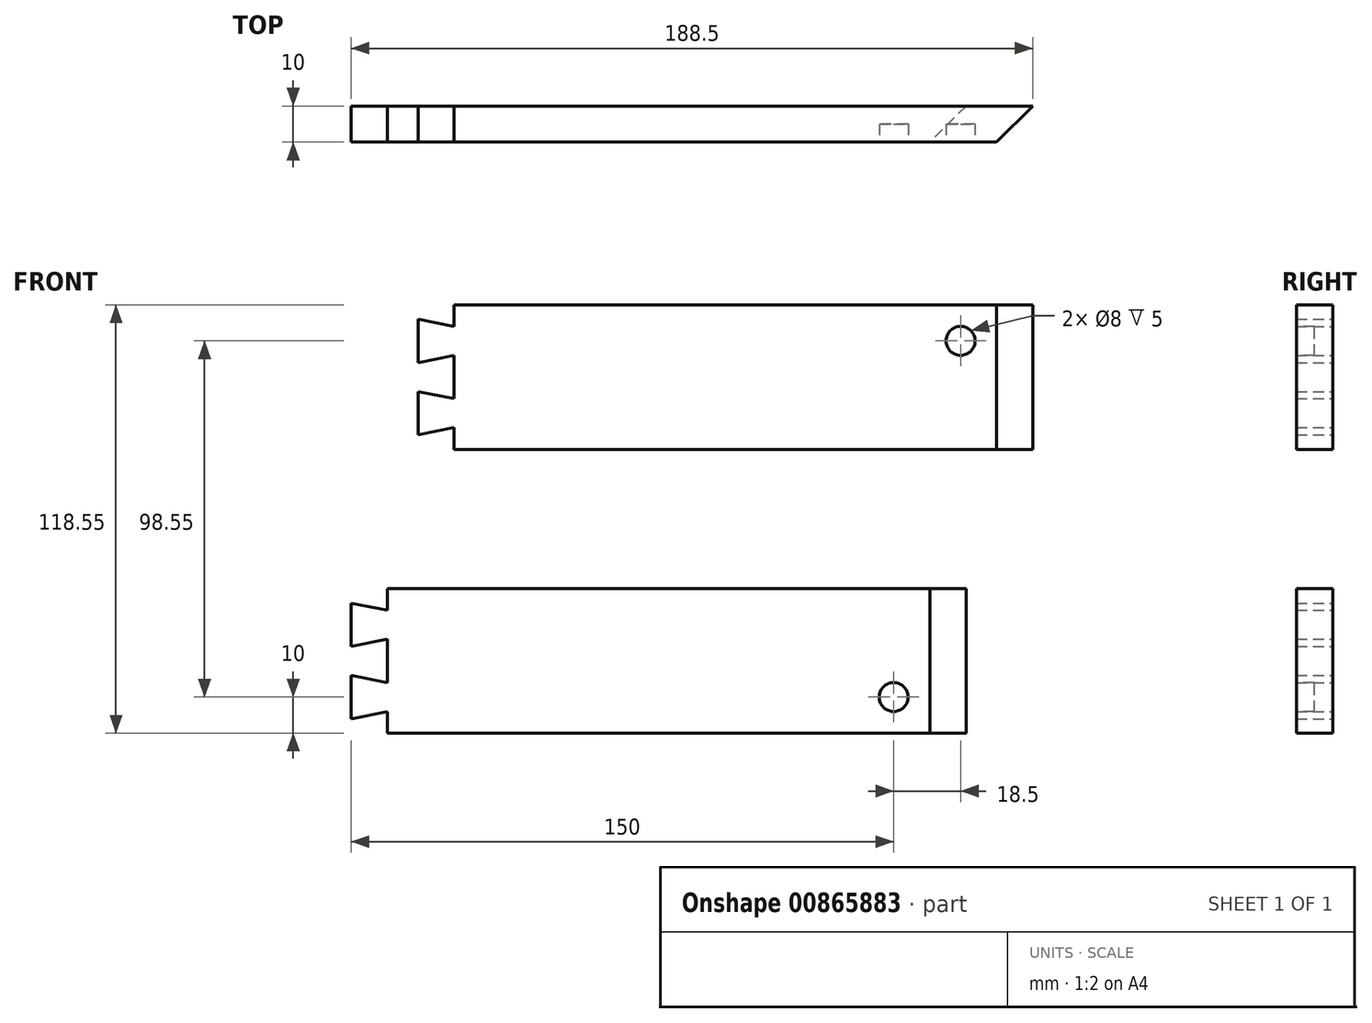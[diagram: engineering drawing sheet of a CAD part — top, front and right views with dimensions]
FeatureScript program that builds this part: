
annotation { "Feature Type Name" : "Feature", "Feature Type Description" : "" }
export const myFeature = defineFeature(function(context is Context, id is Id, definition is map)
    precondition{}
    {
        {
            var Q0;
            Q0=qCreatedBy(makeId("Front.planeOp"),FACE);
            var sketch = newSketch(context, id + "F0", { "sketchPlane" : qUnion([Q0])});
            skLineSegment(sketch, "E0.bottom", {"start": v(10, 0) * mm, "end": v(170, 0) * mm});
            skLineSegment(sketch, "E0.top", {"start": v(10, 40) * mm, "end": v(170, 40) * mm});
            skLineSegment(sketch, "E0.left", {"start": v(0, 4) * mm, "end": v(0, 16) * mm});
            skLineSegment(sketch, "E0.right", {"start": v(170, 0) * mm, "end": v(170, 40) * mm});
            skLineSegment(sketch, "E1", {"start": v(10, 40) * mm, "end": v(10, 34) * mm});
            skLineSegment(sketch, "E2", {"start": v(0, 36) * mm, "end": v(10, 34) * mm});
            skLineSegment(sketch, "E3", {"start": v(0, 24) * mm, "end": v(10, 26) * mm});
            skLineSegment(sketch, "E4", {"start": v(0, 4) * mm, "end": v(10, 6) * mm});
            skLineSegment(sketch, "E5", {"start": v(0, 16) * mm, "end": v(10, 14) * mm});
            skPoint(sketch, "E6.orphan", {"position": v(0, 40) * mm});
            skLineSegment(sketch, "E7.trimOffspring", {"start": v(10, 26) * mm, "end": v(10, 14) * mm});
            skLineSegment(sketch, "E8.trimOffspring", {"start": v(0, 24) * mm, "end": v(0, 36) * mm});
            skLineSegment(sketch, "E9.trimOffspring", {"start": v(10, 6) * mm, "end": v(10, 0) * mm});
            skPoint(sketch, "E10.orphan", {"position": v(0, 0) * mm});
            skLineSegment(sketch, "E11.bottom", {"start": v(-8.5, -78.55) * mm, "end": v(151.5, -78.55) * mm});
            skLineSegment(sketch, "E11.top", {"start": v(-8.5, -38.55) * mm, "end": v(151.5, -38.55) * mm});
            skLineSegment(sketch, "E11.left", {"start": v(-18.5, -74.55) * mm, "end": v(-18.5, -62.55) * mm});
            skLineSegment(sketch, "E11.right", {"start": v(151.5, -78.55) * mm, "end": v(151.5, -38.55) * mm});
            skLineSegment(sketch, "E12", {"start": v(-8.5, -38.55) * mm, "end": v(-8.5, -44.55) * mm});
            skLineSegment(sketch, "E13", {"start": v(-18.5, -42.55) * mm, "end": v(-8.5, -44.55) * mm});
            skLineSegment(sketch, "E14", {"start": v(-18.5, -54.55) * mm, "end": v(-8.5, -52.55) * mm});
            skLineSegment(sketch, "E15", {"start": v(-18.5, -74.55) * mm, "end": v(-8.5, -72.55) * mm});
            skLineSegment(sketch, "E16", {"start": v(-18.5, -62.55) * mm, "end": v(-8.5, -64.55) * mm});
            skPoint(sketch, "E17.orphan", {"position": v(-18.5, -38.55) * mm});
            skLineSegment(sketch, "E18.trimOffspring", {"start": v(-8.5, -52.55) * mm, "end": v(-8.5, -64.55) * mm});
            skLineSegment(sketch, "E19.trimOffspring", {"start": v(-18.5, -54.55) * mm, "end": v(-18.5, -42.55) * mm});
            skLineSegment(sketch, "E20.trimOffspring", {"start": v(-8.5, -72.55) * mm, "end": v(-8.5, -78.55) * mm});
            skPoint(sketch, "E21.orphan", {"position": v(-18.5, -78.55) * mm});
            skSolve(sketch);
        }
        {
            var Q0;
            Q0 = qSketchRegion(id + "F0", true);
            extrude(context, id + "F1", {"entities" : qUnion([Q0]), "depth" : 10 * mm, "offsetDistance" : 25 * mm});
        }
        {
            var Q0;
            Q0=makeQuery(id+"F1.opExtrude","CAP_EDGE",EDGE,{"disambiguationData":[OSD([sQuery(id+"F0.wireOp",EDGE,"E0.right")])],"isStart":false});
            chamfer(context, id + "F2", {"entities" : qUnion([Q0]), "width" : 10 * mm, "tangentPropagation" : true});
        }
        {
            var Q0;
            Q0=makeQuery(id+"F1.opExtrude","CAP_EDGE",EDGE,{"disambiguationData":[OSD([sQuery(id+"F0.wireOp",EDGE,"E11.right")])],"isStart":false});
            chamfer(context, id + "F3", {"entities" : qUnion([Q0]), "width" : 10 * mm, "tangentPropagation" : true});
        }
        {
            var Q0;
            Q0=makeQuery(id+"F1.opExtrude","CAP_FACE",FACE,{"disambiguationData":[OSD([sQuery(id+"F0.wireOp",EDGE,"E0.bottom"),sQuery(id+"F0.wireOp",EDGE,"E0.top"),sQuery(id+"F0.wireOp",EDGE,"E0.left"),sQuery(id+"F0.wireOp",EDGE,"E0.right"),sQuery(id+"F0.wireOp",EDGE,"E1"),sQuery(id+"F0.wireOp",EDGE,"E2"),sQuery(id+"F0.wireOp",EDGE,"E3"),sQuery(id+"F0.wireOp",EDGE,"E4"),sQuery(id+"F0.wireOp",EDGE,"E5"),sQuery(id+"F0.wireOp",EDGE,"E7.trimOffspring"),sQuery(id+"F0.wireOp",EDGE,"E8.trimOffspring"),sQuery(id+"F0.wireOp",EDGE,"E9.trimOffspring")])],"isStart":false});
            var sketch = newSketch(context, id + "F4", { "sketchPlane" : qUnion([Q0])});
            skCircle(sketch, "E22", {"center": v(150, 30) * mm, "radius": 4 * mm});
            skSolve(sketch);
        }
        {
            var Q0;
            Q0 = qSketchRegion(id + "F4", true);
            extrude(context, id + "F5", {"entities" : qUnion([Q0]), "operationType" : NewBodyOperationType.REMOVE, "oppositeDirection" : true, "depth" : 5 * mm, "offsetDistance" : 25 * mm});
        }
        {
            var Q0;
            Q0=makeQuery(id+"F1.opExtrude","CAP_FACE",FACE,{"disambiguationData":[OSD([sQuery(id+"F0.wireOp",EDGE,"E11.bottom"),sQuery(id+"F0.wireOp",EDGE,"E11.top"),sQuery(id+"F0.wireOp",EDGE,"E11.left"),sQuery(id+"F0.wireOp",EDGE,"E11.right"),sQuery(id+"F0.wireOp",EDGE,"E12"),sQuery(id+"F0.wireOp",EDGE,"E13"),sQuery(id+"F0.wireOp",EDGE,"E14"),sQuery(id+"F0.wireOp",EDGE,"E15"),sQuery(id+"F0.wireOp",EDGE,"E16"),sQuery(id+"F0.wireOp",EDGE,"E18.trimOffspring"),sQuery(id+"F0.wireOp",EDGE,"E19.trimOffspring"),sQuery(id+"F0.wireOp",EDGE,"E20.trimOffspring")])],"isStart":false});
            var sketch = newSketch(context, id + "F6", { "sketchPlane" : qUnion([Q0])});
            skCircle(sketch, "E23", {"center": v(131.5, -68.55) * mm, "radius": 4 * mm});
            skSolve(sketch);
        }
        {
            var Q0;
            Q0 = qSketchRegion(id + "F6", true);
            extrude(context, id + "F7", {"entities" : qUnion([Q0]), "operationType" : NewBodyOperationType.REMOVE, "oppositeDirection" : true, "depth" : 5 * mm, "offsetDistance" : 25 * mm});
        }
    });
